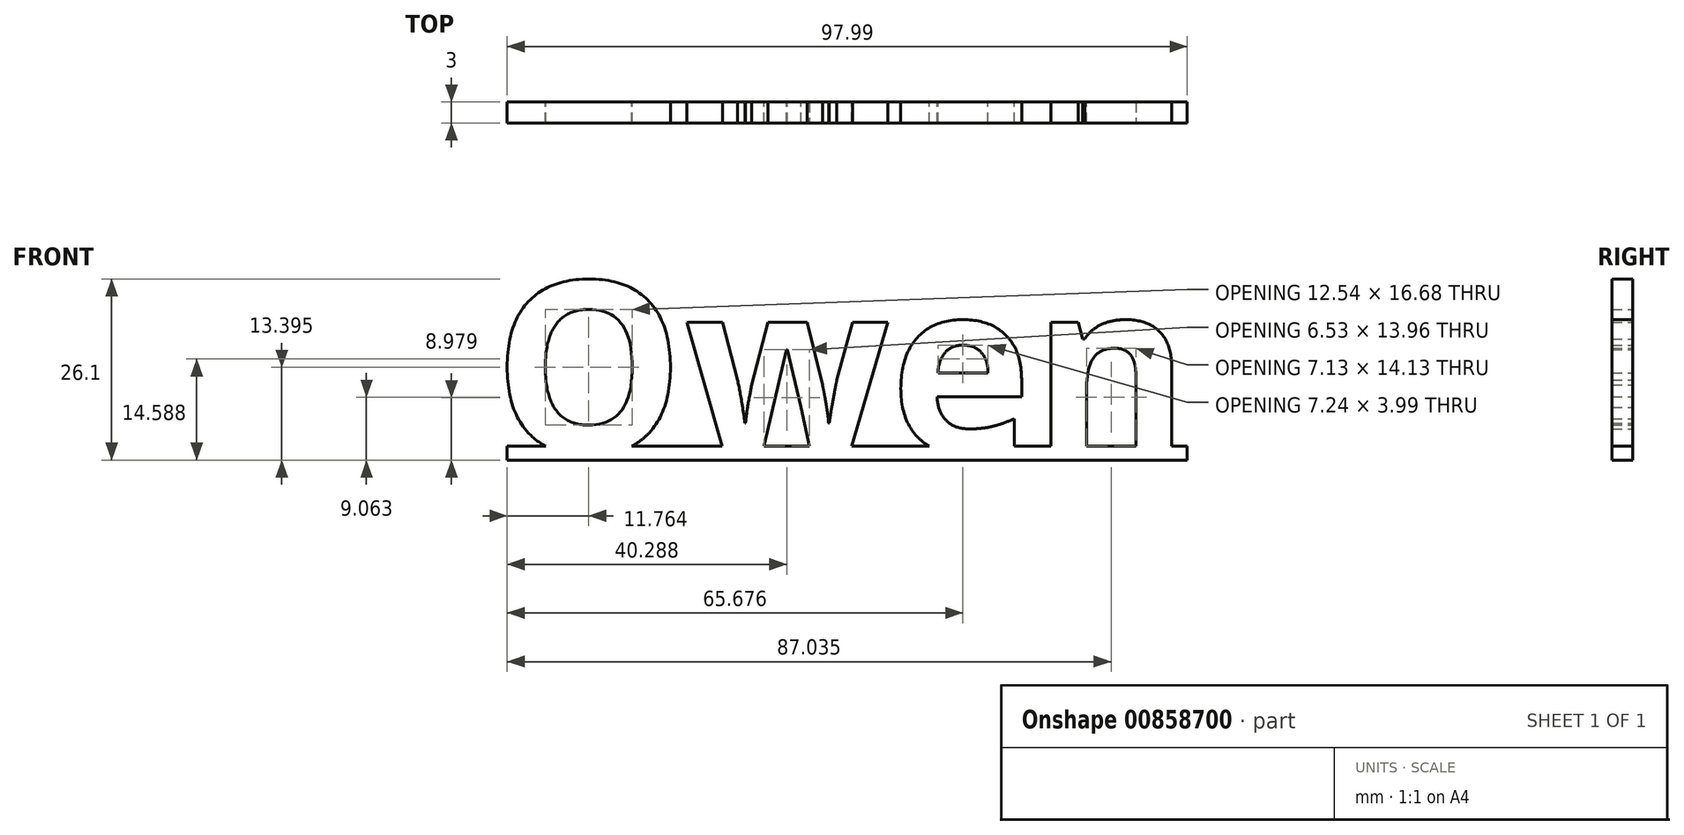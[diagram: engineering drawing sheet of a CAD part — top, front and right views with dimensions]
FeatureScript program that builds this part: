
annotation { "Feature Type Name" : "Feature", "Feature Type Description" : "" }
export const myFeature = defineFeature(function(context is Context, id is Id, definition is map)
    precondition{}
    {
        {
            var Q0;
            Q0=qCreatedBy(makeId("Front.planeOp"),FACE);
            var sketch = newSketch(context, id + "F0", { "sketchPlane" : qUnion([Q0])});
            skText(sketch, "E0", { "text": "Owen", "fontName": "OpenSans-Bold.ttf"});
            const initialGuessF0  = {"E0": [-0.04112, 0, 1, 0, 0.02492]};
            skSetInitialGuess(sketch, initialGuessF0);
            skSolve(sketch);
        }
        {
            var Q0;
            Q0=makeQuery(id+"F0.imprint","IMPRINT",FACE,{"disambiguationData":[TD([[makeQuery(id+"F0.imprint","IMPRINT",EDGE,{"derivedFrom":sQuery(id+"F0.wireOp",EDGE,"E0.sketch_text.stroke-14")}),-1.0]])]});
            var Q1;
            Q1=makeQuery(id+"F0.imprint","IMPRINT",FACE,{"disambiguationData":[TD([[makeQuery(id+"F0.imprint","IMPRINT",EDGE,{"derivedFrom":sQuery(id+"F0.wireOp",EDGE,"E0.sketch_text.stroke-60")}),-1.0]])]});
            var Q2;
            Q2=makeQuery(id+"F0.imprint","IMPRINT",FACE,{"disambiguationData":[TD([[makeQuery(id+"F0.imprint","IMPRINT",EDGE,{"derivedFrom":sQuery(id+"F0.wireOp",EDGE,"E0.sketch_text.stroke-40")}),-1.0]])]});
            var Q3;
            Q3=makeQuery(id+"F0.imprint","IMPRINT",FACE,{"disambiguationData":[TD([[makeQuery(id+"F0.imprint","IMPRINT",EDGE,{"derivedFrom":sQuery(id+"F0.wireOp",EDGE,"E0.sketch_text.stroke-0")}),-1.0]])]});
            extrude(context, id + "F1", {"entities" : qUnion([Q0, Q1, Q2, Q3]), "depth" : 3 * mm, "offsetDistance" : 25.4 * mm});
        }
        {
            var Q0;
            Q0=makeQuery(id+"F1.opExtrude","CAP_FACE",FACE,{"disambiguationData":[OSD([sQuery(id+"F0.wireOp",EDGE,"E0.sketch_text.stroke-0"),sQuery(id+"F0.wireOp",EDGE,"E0.sketch_text.stroke-1"),sQuery(id+"F0.wireOp",EDGE,"E0.sketch_text.stroke-2"),sQuery(id+"F0.wireOp",EDGE,"E0.sketch_text.stroke-3"),sQuery(id+"F0.wireOp",EDGE,"E0.sketch_text.stroke-4"),sQuery(id+"F0.wireOp",EDGE,"E0.sketch_text.stroke-5"),sQuery(id+"F0.wireOp",EDGE,"E0.sketch_text.stroke-6"),sQuery(id+"F0.wireOp",EDGE,"E0.sketch_text.stroke-7"),sQuery(id+"F0.wireOp",EDGE,"E0.sketch_text.stroke-8"),sQuery(id+"F0.wireOp",EDGE,"E0.sketch_text.stroke-9"),sQuery(id+"F0.wireOp",EDGE,"E0.sketch_text.stroke-10"),sQuery(id+"F0.wireOp",EDGE,"E0.sketch_text.stroke-11"),sQuery(id+"F0.wireOp",EDGE,"E0.sketch_text.stroke-12"),sQuery(id+"F0.wireOp",EDGE,"E0.sketch_text.stroke-13")])],"isStart":false});
            var sketch = newSketch(context, id + "F2", { "sketchPlane" : qUnion([Q0])});
            skLineSegment(sketch, "E1.bottom", {"start": v(-39.1, 1) * mm, "end": v(58.88, 1) * mm});
            skLineSegment(sketch, "E1.top", {"start": v(-39.1, -1) * mm, "end": v(58.88, -1) * mm});
            skLineSegment(sketch, "E1.left", {"start": v(-39.1, 1) * mm, "end": v(-39.1, -1) * mm});
            skLineSegment(sketch, "E1.right", {"start": v(58.88, 1) * mm, "end": v(58.88, -1) * mm});
            skSolve(sketch);
        }
        {
            var Q0;
            Q0 = qSketchRegion(id + "F2", true);
            extrude(context, id + "F3", {"entities" : qUnion([Q0]), "operationType" : NewBodyOperationType.ADD, "oppositeDirection" : true, "depth" : 3 * mm, "offsetDistance" : 25.4 * mm});
        }
    });
